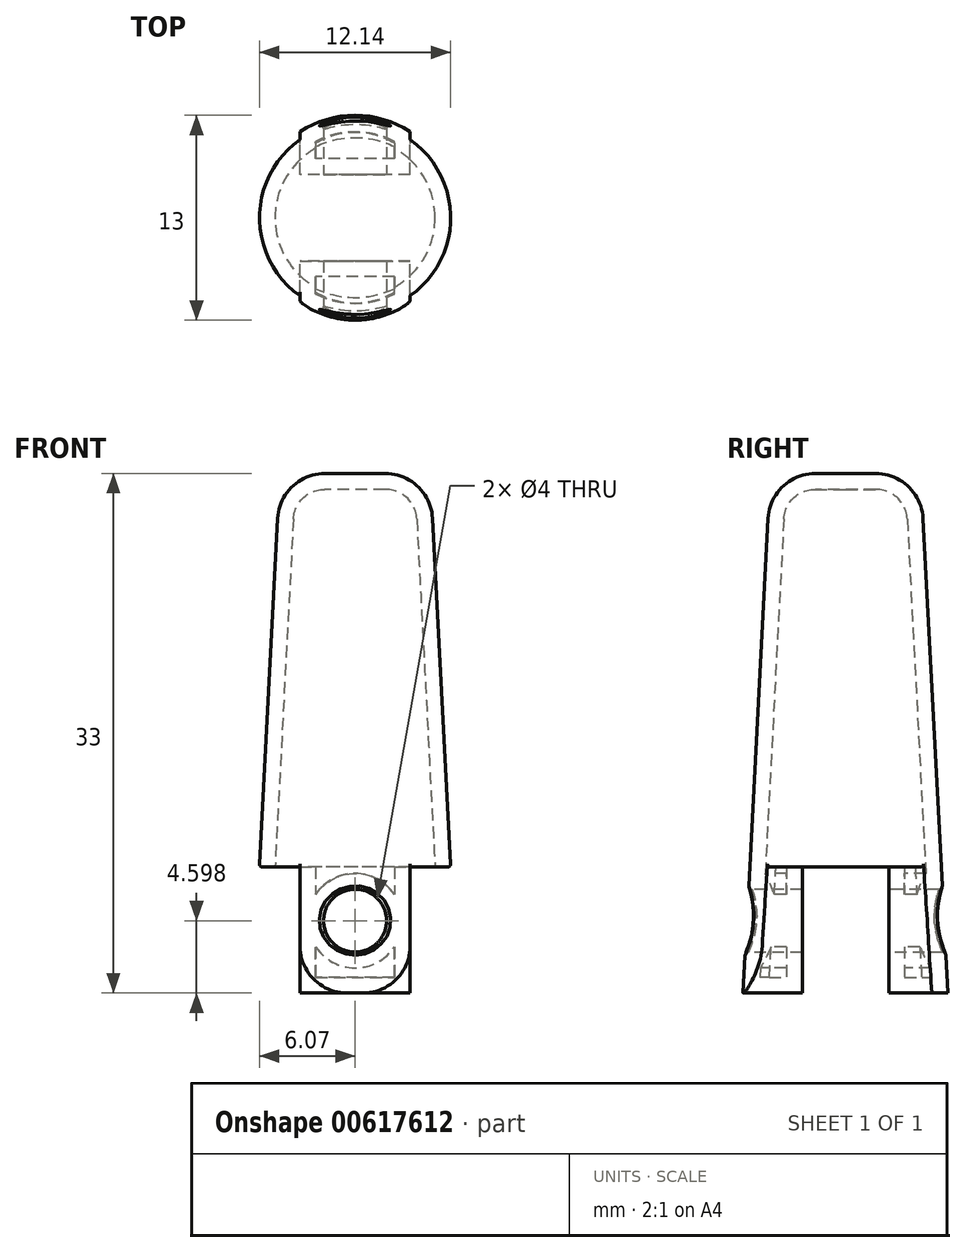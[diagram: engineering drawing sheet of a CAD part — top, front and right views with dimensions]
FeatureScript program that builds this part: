
annotation { "Feature Type Name" : "Feature", "Feature Type Description" : "" }
export const myFeature = defineFeature(function(context is Context, id is Id, definition is map)
    precondition{}
    {
        {
            var Q0;
            Q0=qCreatedBy(makeId("Top.planeOp"),FACE);
            var sketch = newSketch(context, id + "F0", { "sketchPlane" : qUnion([Q0])});
            skCircle(sketch, "E0", {"center": v(0, 0) * mm, "radius": 6.5 * mm});
            skSolve(sketch);
        }
        {
            var Q0;
            Q0=qSketchRegion(id+"F0",true);
            extrude(context, id + "F1", {"entities" : qUnion([Q0]), "depth" : 33 * mm, "offsetDistance" : 25 * mm, "hasDraft" : true, "draftAngle" : 3 * degree, "draftPullDirection" : true});
        }
        {
            var Q0;
            Q0=makeQuery(id+"F1.opExtrude","CAP_EDGE",EDGE,{"disambiguationData":[OSD([sQuery(id+"F0.wireOp",EDGE,"E0")])],"isStart":false});
            fillet(context, id + "F2", {"entities" : qUnion([Q0]), "radius" : 3 * mm, "tangentPropagation" : true, "allowEdgeOverflow" : false});
        }
        {
            var Q0;
            Q0=qCreatedBy(makeId("Top.planeOp"),FACE);
            var sketch = newSketch(context, id + "F3", { "sketchPlane" : qUnion([Q0])});
            skLineSegment(sketch, "E1.bottom", {"start": v(5, -2.75) * mm, "end": v(-5, -2.75) * mm});
            skLineSegment(sketch, "E1.top", {"start": v(5, 2.75) * mm, "end": v(-5, 2.75) * mm});
            skLineSegment(sketch, "E1.left", {"start": v(5, -2.75) * mm, "end": v(5, 2.75) * mm});
            skLineSegment(sketch, "E1.right", {"start": v(-5, -2.75) * mm, "end": v(-5, 2.75) * mm});
            skPoint(sketch, "E1.middle", {"position": v(0, 0) * mm});
            skLineSegment(sketch, "E2.bottom", {"start": v(6.5, -6.25) * mm, "end": v(3.5, -6.25) * mm});
            skLineSegment(sketch, "E2.top", {"start": v(6.5, 6.25) * mm, "end": v(3.5, 6.25) * mm});
            skLineSegment(sketch, "E2.left", {"start": v(6.5, -6.25) * mm, "end": v(6.5, 6.25) * mm});
            skLineSegment(sketch, "E2.right", {"start": v(3.5, -6.25) * mm, "end": v(3.5, 6.25) * mm});
            skPoint(sketch, "E2.middle", {"position": v(5, 0) * mm});
            skLineSegment(sketch, "E3.bottom", {"start": v(-3.5, -6.25) * mm, "end": v(-6.5, -6.25) * mm});
            skLineSegment(sketch, "E3.top", {"start": v(-3.5, 6.25) * mm, "end": v(-6.5, 6.25) * mm});
            skLineSegment(sketch, "E3.left", {"start": v(-3.5, -6.25) * mm, "end": v(-3.5, 6.25) * mm});
            skLineSegment(sketch, "E3.right", {"start": v(-6.5, -6.25) * mm, "end": v(-6.5, 6.25) * mm});
            skPoint(sketch, "E3.middle", {"position": v(-5, 0) * mm});
            skSolve(sketch);
        }
        {
            var Q0;
            Q0=qSketchRegion(id+"F3",true);
            extrude(context, id + "F4", {"entities" : qUnion([Q0]), "operationType" : NewBodyOperationType.REMOVE, "depth" : 8 * mm, "offsetDistance" : 25 * mm});
        }
        {
            var Q0;
            Q0=makeQuery(id+"F4.boolean.opBoolean","COPY",FACE,{"derivedFrom":makeQuery(id+"F4.opExtrude","SWEPT_FACE",FACE,{"disambiguationData":[OSD([sQuery(id+"F3.wireOp",EDGE,"E1.bottom")])]})});
            var sketch = newSketch(context, id + "F5", { "sketchPlane" : qUnion([Q0])});
            skCircle(sketch, "E4", {"center": v(0, 4.6) * mm, "radius": 2 * mm});
            skPoint(sketch, "E4.centerSnap0", {"position": v(0, 8) * mm});
            skSolve(sketch);
        }
        {
            var Q0;
            Q0=qSketchRegion(id+"F5",true);
            extrude(context, id + "F6", {"entities" : qUnion([Q0]), "operationType" : NewBodyOperationType.REMOVE, "depth" : 25 * mm, "offsetDistance" : 25 * mm, "hasSecondDirection" : true, "secondDirectionOppositeDirection" : true, "secondDirectionDepth" : 25 * mm});
        }
        {
            var Q0;
            Q0=makeQuery(id+"F4.boolean.opBoolean","COPY",FACE,{"derivedFrom":makeQuery(id+"F4.opExtrude","CAP_FACE",FACE,{"disambiguationData":[OSD([sQuery(id+"F3.wireOp",EDGE,"E1.bottom"),sQuery(id+"F3.wireOp",EDGE,"E1.top"),sQuery(id+"F3.wireOp",EDGE,"E2.bottom"),sQuery(id+"F3.wireOp",EDGE,"E2.top"),sQuery(id+"F3.wireOp",EDGE,"E2.left"),sQuery(id+"F3.wireOp",EDGE,"E2.right"),sQuery(id+"F3.wireOp",EDGE,"E3.bottom"),sQuery(id+"F3.wireOp",EDGE,"E3.top"),sQuery(id+"F3.wireOp",EDGE,"E3.left"),sQuery(id+"F3.wireOp",EDGE,"E3.right")])],"isStart":false})});
            shell(context, id + "F7", {"entities" : qUnion([Q0]), "thickness" : 1 * mm});
        }
        {
            var Q0;
            Q0=makeQuery(id+"F6.boolean.opBoolean","INTERSECT",EDGE,{"disambiguationData":[OD(1.0)],"derivedFrom":[makeQuery(id+"F1.opExtrude","SWEPT_FACE",FACE,{"disambiguationData":[OSD([sQuery(id+"F0.wireOp",EDGE,"E0")])]}),makeQuery(id+"F6.opExtrude","SWEPT_FACE",FACE,{"disambiguationData":[OSD([sQuery(id+"F5.wireOp",EDGE,"E4")])]})]});
            var Q1;
            Q1=makeQuery(id+"F6.boolean.opBoolean","INTERSECT",EDGE,{"disambiguationData":[OD(0.0)],"derivedFrom":[makeQuery(id+"F1.opExtrude","SWEPT_FACE",FACE,{"disambiguationData":[OSD([sQuery(id+"F0.wireOp",EDGE,"E0")])]}),makeQuery(id+"F6.opExtrude","SWEPT_FACE",FACE,{"disambiguationData":[OSD([sQuery(id+"F5.wireOp",EDGE,"E4")])]})]});
            var Q2;
            Q2=makeQuery(id+"F4.boolean.opBoolean","INTERSECT",EDGE,{"disambiguationData":[OD(1.0)],"derivedFrom":[makeQuery(id+"F1.opExtrude","SWEPT_FACE",FACE,{"disambiguationData":[OSD([sQuery(id+"F0.wireOp",EDGE,"E0")])]}),makeQuery(id+"F4.opExtrude","CAP_FACE",FACE,{"disambiguationData":[OSD([sQuery(id+"F3.wireOp",EDGE,"E1.bottom"),sQuery(id+"F3.wireOp",EDGE,"E1.top"),sQuery(id+"F3.wireOp",EDGE,"E2.bottom"),sQuery(id+"F3.wireOp",EDGE,"E2.top"),sQuery(id+"F3.wireOp",EDGE,"E2.left"),sQuery(id+"F3.wireOp",EDGE,"E2.right"),sQuery(id+"F3.wireOp",EDGE,"E3.bottom"),sQuery(id+"F3.wireOp",EDGE,"E3.top"),sQuery(id+"F3.wireOp",EDGE,"E3.left"),sQuery(id+"F3.wireOp",EDGE,"E3.right")])],"isStart":false})]});
            var Q3;
            Q3=makeQuery(id+"F4.boolean.opBoolean","INTERSECT",EDGE,{"disambiguationData":[OD(0.0)],"derivedFrom":[makeQuery(id+"F1.opExtrude","SWEPT_FACE",FACE,{"disambiguationData":[OSD([sQuery(id+"F0.wireOp",EDGE,"E0")])]}),makeQuery(id+"F4.opExtrude","CAP_FACE",FACE,{"disambiguationData":[OSD([sQuery(id+"F3.wireOp",EDGE,"E1.bottom"),sQuery(id+"F3.wireOp",EDGE,"E1.top"),sQuery(id+"F3.wireOp",EDGE,"E2.bottom"),sQuery(id+"F3.wireOp",EDGE,"E2.top"),sQuery(id+"F3.wireOp",EDGE,"E2.left"),sQuery(id+"F3.wireOp",EDGE,"E2.right"),sQuery(id+"F3.wireOp",EDGE,"E3.bottom"),sQuery(id+"F3.wireOp",EDGE,"E3.top"),sQuery(id+"F3.wireOp",EDGE,"E3.left"),sQuery(id+"F3.wireOp",EDGE,"E3.right")])],"isStart":false})]});
            fillet(context, id + "F8", {"entities" : qUnion([Q0, Q1, Q2, Q3]), "radius" : 0.2 * mm, "tangentPropagation" : true, "allowEdgeOverflow" : false});
        }
        {
            var Q0;
            {var subQ0=sQuery(id+"F3.wireOp",EDGE,"E2.right");Q0=makeQuery(id+"F4.boolean.opBoolean","COPY",EDGE,{"derivedFrom":makeQuery(id+"F4.opExtrude","CAP_EDGE",EDGE,{"disambiguationData":[OSD([subQ0]),TDD([makeQuery(id+"F3.imprint","IMPRINT",EDGE,{"disambiguationData":[TD([[makeQuery(id+"F3.imprint","INTERSECT",VERTEX,{"derivedFrom":[sQuery(id+"F3.wireOp",EDGE,"E2.bottom"),subQ0]}),-1.0]])],"derivedFrom":subQ0})])],"isStart":true})});}
            var Q1;
            {var subQ0=sQuery(id+"F3.wireOp",EDGE,"E2.right");Q1=makeQuery(id+"F4.boolean.opBoolean","COPY",EDGE,{"derivedFrom":makeQuery(id+"F4.opExtrude","CAP_EDGE",EDGE,{"disambiguationData":[OSD([subQ0]),TDD([makeQuery(id+"F3.imprint","IMPRINT",EDGE,{"disambiguationData":[TD([[makeQuery(id+"F3.imprint","INTERSECT",VERTEX,{"derivedFrom":[sQuery(id+"F3.wireOp",EDGE,"E2.top"),subQ0]}),1.0]])],"derivedFrom":subQ0})])],"isStart":true})});}
            var Q2;
            {var subQ0=sQuery(id+"F3.wireOp",EDGE,"E3.left");Q2=makeQuery(id+"F4.boolean.opBoolean","COPY",EDGE,{"derivedFrom":makeQuery(id+"F4.opExtrude","CAP_EDGE",EDGE,{"disambiguationData":[OSD([subQ0]),TDD([makeQuery(id+"F3.imprint","IMPRINT",EDGE,{"disambiguationData":[TD([[makeQuery(id+"F3.imprint","INTERSECT",VERTEX,{"derivedFrom":[sQuery(id+"F3.wireOp",EDGE,"E3.top"),subQ0]}),1.0]])],"derivedFrom":subQ0})])],"isStart":true})});}
            var Q3;
            {var subQ0=sQuery(id+"F3.wireOp",EDGE,"E3.left");Q3=makeQuery(id+"F4.boolean.opBoolean","COPY",EDGE,{"derivedFrom":makeQuery(id+"F4.opExtrude","CAP_EDGE",EDGE,{"disambiguationData":[OSD([subQ0]),TDD([makeQuery(id+"F3.imprint","IMPRINT",EDGE,{"disambiguationData":[TD([[makeQuery(id+"F3.imprint","INTERSECT",VERTEX,{"derivedFrom":[sQuery(id+"F3.wireOp",EDGE,"E3.bottom"),subQ0]}),-1.0]])],"derivedFrom":subQ0})])],"isStart":true})});}
            fillet(context, id + "F9", {"entities" : qUnion([Q0, Q1, Q2, Q3]), "radius" : 3 * mm, "tangentPropagation" : true, "allowEdgeOverflow" : false});
        }
    });
